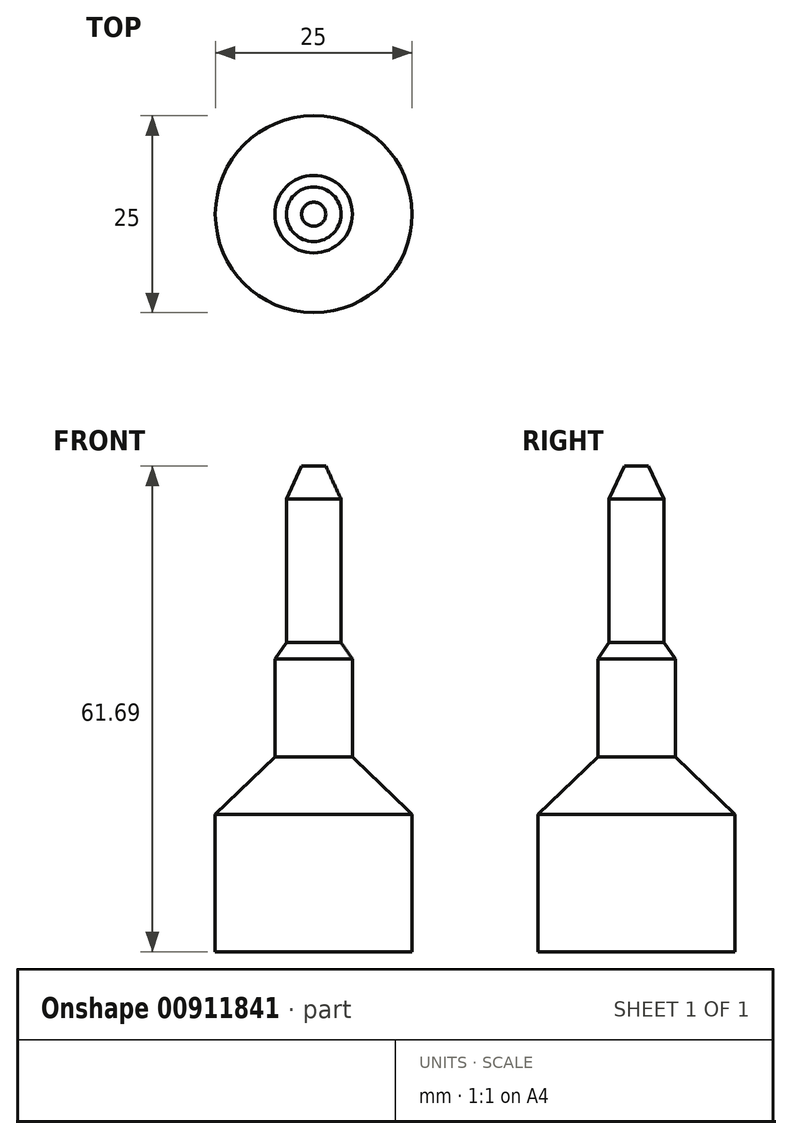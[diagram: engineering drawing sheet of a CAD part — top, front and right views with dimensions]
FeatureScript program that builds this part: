
annotation { "Feature Type Name" : "Feature", "Feature Type Description" : "" }
export const myFeature = defineFeature(function(context is Context, id is Id, definition is map)
    precondition{}
    {
        {
            var Q0;
            Q0=qCreatedBy(makeId("Front.planeOp"),FACE);
            var sketch = newSketch(context, id + "F0", { "sketchPlane" : qUnion([Q0])});
            skLineSegment(sketch, "E0.bottom", {"start": v(0, -81.13) * mm, "end": v(-12.5, -81.13) * mm});
            skLineSegment(sketch, "E0.top", {"start": v(0, -63.71) * mm, "end": v(-12.5, -63.71) * mm});
            skLineSegment(sketch, "E0.left", {"start": v(0, -81.13) * mm, "end": v(0, -63.71) * mm});
            skLineSegment(sketch, "E0.right", {"start": v(-12.5, -81.13) * mm, "end": v(-12.5, -63.71) * mm});
            skLineSegment(sketch, "E1", {"start": v(-12.5, -63.71) * mm, "end": v(-4.92, -56.38) * mm});
            skLineSegment(sketch, "E2", {"start": v(-4.92, -56.38) * mm, "end": v(-4.92, -43.96) * mm});
            skLineSegment(sketch, "E3", {"start": v(-4.92, -43.96) * mm, "end": v(-3.47, -41.86) * mm});
            skLineSegment(sketch, "E4", {"start": v(-3.47, -41.86) * mm, "end": v(-3.47, -23.63) * mm});
            skLineSegment(sketch, "E5", {"start": v(-3.47, -23.63) * mm, "end": v(-1.53, -19.44) * mm});
            skLineSegment(sketch, "E6", {"start": v(-1.53, -19.44) * mm, "end": v(0, -19.44) * mm});
            skLineSegment(sketch, "E7", {"start": v(0, -19.44) * mm, "end": v(0, -63.71) * mm});
            skLineSegment(sketch, "E8", {"start": v(0, -8.8) * mm, "end": v(0, -85.25) * mm});
            skSolve(sketch);
        }
        {
            var Q0;
            Q0 = qSketchRegion(id + "F0", true);
            var Q1;
            Q1=sQuery(id+"F0.wireOp",EDGE,"E8");
            revolve(context, id + "F1", {"surfaceOperationType" : NewSurfaceOperationType.NEW, "entities" : qUnion([Q0]), "axis" : qUnion([Q1]), "revolveType" : RevolveType.FULL});
        }
    });
